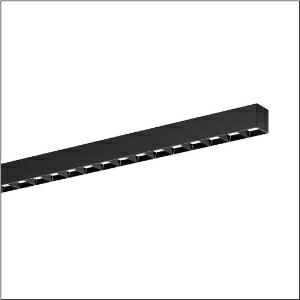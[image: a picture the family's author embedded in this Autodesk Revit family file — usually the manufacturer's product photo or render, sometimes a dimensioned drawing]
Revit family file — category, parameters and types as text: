
# Revit family: silica_r__21_51mx21dc4abb_1522
name_source: partatom
category: Lighting Fixtures
units: mm (PartAtom-declared; Revit-internal decimal feet)

## family parameters
Cut with Voids When Loaded = No
Host = Face
Light Source = No
Part Type = Normal
Room Calculation Point = No
Round Connector Dimension = Use Diameter
Shared = No

## types (1)
- --- (1 x LED, 10800 lm, 64.8 W, 4000K)
    Apparent Load = 65 VA
    CIE Flux Codes = 87 99 100 100 100
    Color Rendering = 80
    Color Temperature = 4000K
    Default Elevation = 1800 mm
    Description = Silica® 21, office luminaire, primary light control with darklight reflector, of PMMA, black, CAT 2 (L<= 3000cd/m²), light emission: direct distribution, primary light characteristic: symmetric, installation type: surface-mounted, LED, rated luminous flux: 10.800lm, luminous efficacy: 167lm/W, light colour: 840, colour temperature: 4000K, with terminal, 3+2-pole, max. 2.5mm², mains connection: 220..240V, AC, 50/60Hz, rated input power: 64.8W, luminaire housing, of aluminium, jet black (RAL 9005), length: 3.004mm, width: 53mm, height: 53mm, protection rating (complete): IP20, insulation class (complete): insulation class I (protective earthing), certification: CE, permissible operating ambient temperature: 0..+35°C, standard: EN 50419, packaging unit: 1 piece
    Height = 0 mm  [stored 0 ft]
    Lamp = 1 x LED
    Lamp Light Flux = 10800 lm
    Lamp Power = 64.8 W
    Lamp count = 1
    Length = 3004 mm
    Luminous efficacy = 167 lm/W
    Manufacturer = Siteco
    ModVariant = No
    Model = 51MX21DC4ABB
    Mounting Place = Ceiling
    Mounting Type = Recessed
    Number of Poles = 1
    OnlyDefault = Yes
    Power Factor = 1
    Product Name = Silica® 21
    Product group = office luminaire | ceiling recessed
    ProductGroupID = 401
    Protection Class = Protection class I
    Protection Degree = IP 20
    RLX_Detail_Level = 1
    RLX_Emergency_Light_Flux = 0 lm
    RLX_Emergency_Type = 0
    RLX_Emergency_Type_DB = No
    RlxData = <blob elided: 63973 chars, md5=73e46c7d>
    Socket = socket
    Standby Power = 0 W
    System Light Flux = 10800 lm
    System Power = 65 W
    Type Comments = factory setting: luminous flux: 100 % | dim-lin: 254 | 367 mA
    Type Image = l_1297756.jpg
    URL = http://relux.com
    VarID = @adj_054569
    Voltage = 0 V
    Weight = 0.00 kg
    Width = 53 mm

note: [stored X ft] marks values corroborated as IEEE doubles in the binary element streams (Revit-internal decimal feet)

## geometry (parser evidence)
native form markers: Blend x4, Sweep x11
no freeform markers — native parametric forms only
